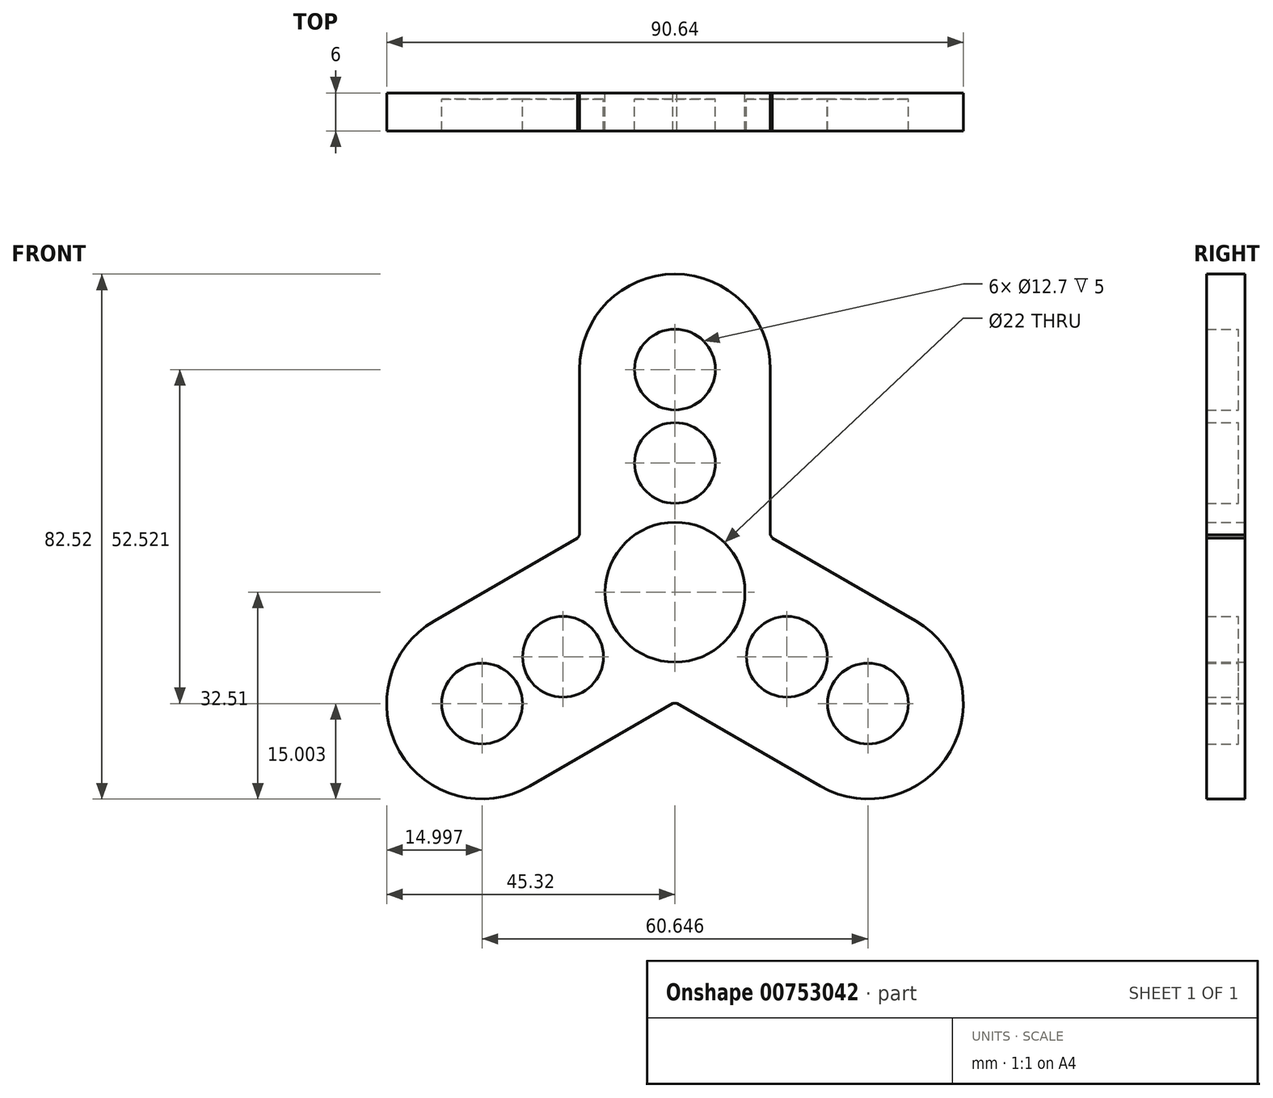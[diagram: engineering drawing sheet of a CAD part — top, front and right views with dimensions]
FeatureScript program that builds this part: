
annotation { "Feature Type Name" : "Feature", "Feature Type Description" : "" }
export const myFeature = defineFeature(function(context is Context, id is Id, definition is map)
    precondition{}
    {
        {
            var Q0;
            Q0=qCreatedBy(makeId("Front.planeOp"),FACE);
            var sketch = newSketch(context, id + "F0", { "sketchPlane" : qUnion([Q0])});
            skCircle(sketch, "E0", {"center": v(0, 0) * mm, "radius": 11 * mm});
            skArc(sketch, "E1", {"start": v(-0.3, -17.5) * mm, "mid": v(0, -17.5) * mm, "end": v(0.3, -17.5) * mm});
            skArc(sketch, "E2", {"start": v(15, 35.01) * mm, "mid": v(0, 50.01) * mm, "end": v(-15, 35.01) * mm});
            skPoint(sketch, "E3.center", {"position": v(0, 0.02) * mm});
            skPoint(sketch, "E4.center", {"position": v(-0.08, 0.03) * mm});
            skLineSegment(sketch, "E5", {"start": v(-15, 35.01) * mm, "end": v(-15, 9.01) * mm});
            skLineSegment(sketch, "E6", {"start": v(15, 9.01) * mm, "end": v(15, 35.01) * mm});
            skLineSegment(sketch, "E7.1.0", {"start": v(-22.82, -30.5) * mm, "end": v(-0.3, -17.5) * mm});
            skArc(sketch, "E7.1.1", {"start": v(-37.82, -4.52) * mm, "mid": v(-43.31, -25) * mm, "end": v(-22.82, -30.5) * mm});
            skLineSegment(sketch, "E7.1.2", {"start": v(-15.3, 8.48) * mm, "end": v(-37.82, -4.52) * mm});
            skLineSegment(sketch, "E7.2.0", {"start": v(37.82, -4.52) * mm, "end": v(15.3, 8.48) * mm});
            skArc(sketch, "E7.2.1", {"start": v(22.82, -30.5) * mm, "mid": v(43.31, -25) * mm, "end": v(37.82, -4.52) * mm});
            skLineSegment(sketch, "E7.2.2", {"start": v(0.3, -17.5) * mm, "end": v(22.82, -30.5) * mm});
            skArc(sketch, "E8.trimOffspring", {"start": v(15.3, 8.48) * mm, "mid": v(15.16, 8.75) * mm, "end": v(15, 9.01) * mm});
            skArc(sketch, "E9.trimOffspring", {"start": v(-15, 9.01) * mm, "mid": v(-15.16, 8.75) * mm, "end": v(-15.3, 8.48) * mm});
            skCircle(sketch, "E10", {"center": v(0, 35.01) * mm, "radius": 6.35 * mm});
            skCircle(sketch, "E11.1.0", {"center": v(0, 20.31) * mm, "radius": 6.35 * mm});
            skPoint(sketch, "E11.center", {"position": v(0, 27.66) * mm});
            skCircle(sketch, "E12.1.0", {"center": v(-30.32, -17.5) * mm, "radius": 6.35 * mm});
            skCircle(sketch, "E12.1.1", {"center": v(-17.6, -10.16) * mm, "radius": 6.35 * mm});
            skCircle(sketch, "E12.2.0", {"center": v(30.32, -17.5) * mm, "radius": 6.35 * mm});
            skCircle(sketch, "E12.2.1", {"center": v(17.6, -10.16) * mm, "radius": 6.35 * mm});
            skSolve(sketch);
        }
        {
            var Q0;
            Q0=makeQuery(id+"F0.imprint","IMPRINT",FACE,{"disambiguationData":[TD([[makeQuery(id+"F0.imprint","IMPRINT",EDGE,{"derivedFrom":sQuery(id+"F0.wireOp",EDGE,"03ac1bf7-c0f5-4b97-b4e3-3a6f48659557.1.0")}),1.0]])]});
            var Q1;
            Q1=makeQuery(id+"F0.imprint","IMPRINT",FACE,{"disambiguationData":[TD([[makeQuery(id+"F0.imprint","IMPRINT",EDGE,{"derivedFrom":sQuery(id+"F0.wireOp",EDGE,"E2")}),1.0]])]});
            extrude(context, id + "F1", {"entities" : qUnion([Q0, Q1]), "depth" : 6 * mm, "offsetDistance" : 25 * mm});
        }
        {
            var Q0;
            Q0=makeQuery(id+"F0.imprint","IMPRINT",FACE,{"disambiguationData":[TD([[makeQuery(id+"F0.imprint","IMPRINT",EDGE,{"derivedFrom":sQuery(id+"F0.wireOp",EDGE,"ozRRsO5K-dEbu-LDsO-T78Q-tp5oNAb8Ttle")}),1.0]])]});
            var Q1;
            Q1=makeQuery(id+"F0.imprint","IMPRINT",FACE,{"disambiguationData":[TD([[makeQuery(id+"F0.imprint","IMPRINT",EDGE,{"derivedFrom":sQuery(id+"F0.wireOp",EDGE,"183276f4-22ff-47bc-930c-d480893e51a8.1.0")}),1.0]])]});
            var Q2;
            Q2=makeQuery(id+"F0.imprint","IMPRINT",FACE,{"disambiguationData":[TD([[makeQuery(id+"F0.imprint","IMPRINT",EDGE,{"derivedFrom":sQuery(id+"F0.wireOp",EDGE,"258c3f14-1087-4e86-bfdb-57bf13d21df8.2.0")}),1.0]])]});
            var Q3;
            Q3=makeQuery(id+"F0.imprint","IMPRINT",FACE,{"disambiguationData":[TD([[makeQuery(id+"F0.imprint","IMPRINT",EDGE,{"derivedFrom":sQuery(id+"F0.wireOp",EDGE,"258c3f14-1087-4e86-bfdb-57bf13d21df8.1.1")}),1.0]])]});
            var Q4;
            Q4=makeQuery(id+"F0.imprint","IMPRINT",FACE,{"disambiguationData":[TD([[makeQuery(id+"F0.imprint","IMPRINT",EDGE,{"derivedFrom":sQuery(id+"F0.wireOp",EDGE,"258c3f14-1087-4e86-bfdb-57bf13d21df8.1.0")}),1.0]])]});
            var Q5;
            Q5=makeQuery(id+"F0.imprint","IMPRINT",FACE,{"disambiguationData":[TD([[makeQuery(id+"F0.imprint","IMPRINT",EDGE,{"derivedFrom":sQuery(id+"F0.wireOp",EDGE,"258c3f14-1087-4e86-bfdb-57bf13d21df8.2.1")}),1.0]])]});
            var Q6;
            Q6=makeQuery(id+"F0.imprint","IMPRINT",FACE,{"disambiguationData":[TD([[makeQuery(id+"F0.imprint","IMPRINT",EDGE,{"derivedFrom":sQuery(id+"F0.wireOp",EDGE,"E12.1.0")}),1.0]])]});
            var Q7;
            Q7=makeQuery(id+"F0.imprint","IMPRINT",FACE,{"disambiguationData":[TD([[makeQuery(id+"F0.imprint","IMPRINT",EDGE,{"derivedFrom":sQuery(id+"F0.wireOp",EDGE,"E12.1.1")}),1.0]])]});
            var Q8;
            Q8=makeQuery(id+"F0.imprint","IMPRINT",FACE,{"disambiguationData":[TD([[makeQuery(id+"F0.imprint","IMPRINT",EDGE,{"derivedFrom":sQuery(id+"F0.wireOp",EDGE,"E12.2.1")}),1.0]])]});
            var Q9;
            Q9=makeQuery(id+"F0.imprint","IMPRINT",FACE,{"disambiguationData":[TD([[makeQuery(id+"F0.imprint","IMPRINT",EDGE,{"derivedFrom":sQuery(id+"F0.wireOp",EDGE,"E12.2.0")}),1.0]])]});
            var Q10;
            Q10=makeQuery(id+"F0.imprint","IMPRINT",FACE,{"disambiguationData":[TD([[makeQuery(id+"F0.imprint","IMPRINT",EDGE,{"derivedFrom":sQuery(id+"F0.wireOp",EDGE,"E11.1.0")}),1.0]])]});
            var Q11;
            Q11=makeQuery(id+"F0.imprint","IMPRINT",FACE,{"disambiguationData":[TD([[makeQuery(id+"F0.imprint","IMPRINT",EDGE,{"derivedFrom":sQuery(id+"F0.wireOp",EDGE,"E10")}),1.0]])]});
            extrude(context, id + "F2", {"entities" : qUnion([Q0, Q1, Q2, Q3, Q4, Q5, Q6, Q7, Q8, Q9, Q10, Q11]), "operationType" : NewBodyOperationType.ADD, "depth" : 1 * mm, "offsetDistance" : 25 * mm});
        }
    });
